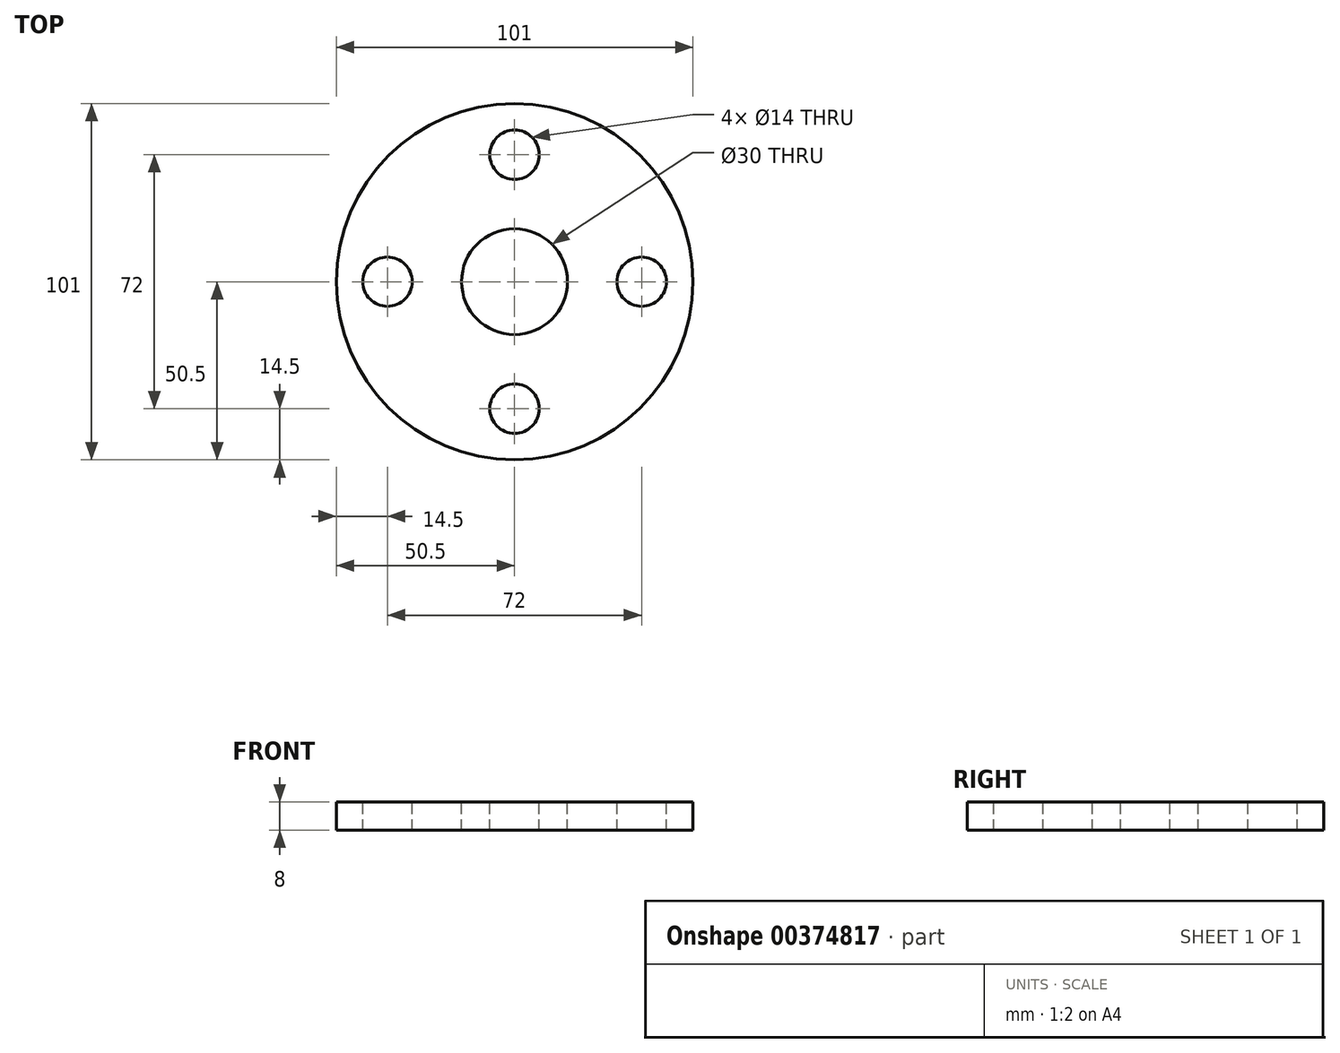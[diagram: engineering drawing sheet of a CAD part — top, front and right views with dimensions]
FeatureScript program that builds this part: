
annotation { "Feature Type Name" : "Feature", "Feature Type Description" : "" }
export const myFeature = defineFeature(function(context is Context, id is Id, definition is map)
    precondition{}
    {
        {
            var Q0;
            Q0=qCreatedBy(makeId("Top.planeOp"),FACE);
            var sketch = newSketch(context, id + "F0", { "sketchPlane" : qUnion([Q0])});
            skCircle(sketch, "E0", {"center": v(0, 0) * mm, "radius": 50.5 * mm});
            skSolve(sketch);
        }
        {
            var Q0;
            Q0 = qSketchRegion(id + "F0", true);
            extrude(context, id + "F1", {"entities" : qUnion([Q0]), "depth" : 8 * mm, "offsetDistance" : 25 * mm});
        }
        {
            var Q0;
            Q0=makeQuery(id+"F1.opExtrude","CAP_FACE",FACE,{"disambiguationData":[OSD([sQuery(id+"F0.wireOp",EDGE,"E0")])],"isStart":false});
            var sketch = newSketch(context, id + "F2", { "sketchPlane" : qUnion([Q0])});
            skCircle(sketch, "E1", {"center": v(0, 0) * mm, "radius": 15 * mm});
            skCircle(sketch, "E2", {"center": v(0, 36) * mm, "radius": 7 * mm});
            skCircle(sketch, "E3.1.0", {"center": v(-36, 0) * mm, "radius": 7 * mm});
            skCircle(sketch, "E3.2.0", {"center": v(0, -36) * mm, "radius": 7 * mm});
            skCircle(sketch, "E4.1.3.0", {"center": v(36, 0) * mm, "radius": 7 * mm});
            skSolve(sketch);
        }
        {
            var Q0;
            Q0=makeQuery(id+"F2.imprint","IMPRINT",FACE,{"disambiguationData":[TD([[makeQuery(id+"F2.imprint","IMPRINT",EDGE,{"derivedFrom":sQuery(id+"F2.wireOp",EDGE,"E3.1.0")}),1.0]])]});
            var Q1;
            Q1=makeQuery(id+"F2.imprint","IMPRINT",FACE,{"disambiguationData":[TD([[makeQuery(id+"F2.imprint","IMPRINT",EDGE,{"derivedFrom":sQuery(id+"F2.wireOp",EDGE,"E2")}),1.0]])]});
            var Q2;
            Q2=makeQuery(id+"F2.imprint","IMPRINT",FACE,{"disambiguationData":[TD([[makeQuery(id+"F2.imprint","IMPRINT",EDGE,{"derivedFrom":sQuery(id+"F2.wireOp",EDGE,"E4.1.3.0")}),1.0]])]});
            var Q3;
            Q3=makeQuery(id+"F2.imprint","IMPRINT",FACE,{"disambiguationData":[TD([[makeQuery(id+"F2.imprint","IMPRINT",EDGE,{"derivedFrom":sQuery(id+"F2.wireOp",EDGE,"E3.2.0")}),1.0]])]});
            var Q4;
            Q4=makeQuery(id+"F2.imprint","IMPRINT",FACE,{"disambiguationData":[TD([[makeQuery(id+"F2.imprint","IMPRINT",EDGE,{"derivedFrom":sQuery(id+"F2.wireOp",EDGE,"E1")}),1.0]])]});
            var Q5;
            Q5=makeQuery(id+"F1.opExtrude","CAP_FACE",FACE,{"disambiguationData":[OSD([sQuery(id+"F0.wireOp",EDGE,"E0")])],"isStart":true});
            extrude(context, id + "F3", {"entities" : qUnion([Q0, Q1, Q2, Q3, Q4]), "operationType" : NewBodyOperationType.REMOVE, "endBound" : BoundingType.UP_TO_SURFACE, "oppositeDirection" : true, "depth" : 25 * mm, "endBoundEntityFace" : qUnion([Q5]), "offsetDistance" : 25 * mm});
        }
    });
